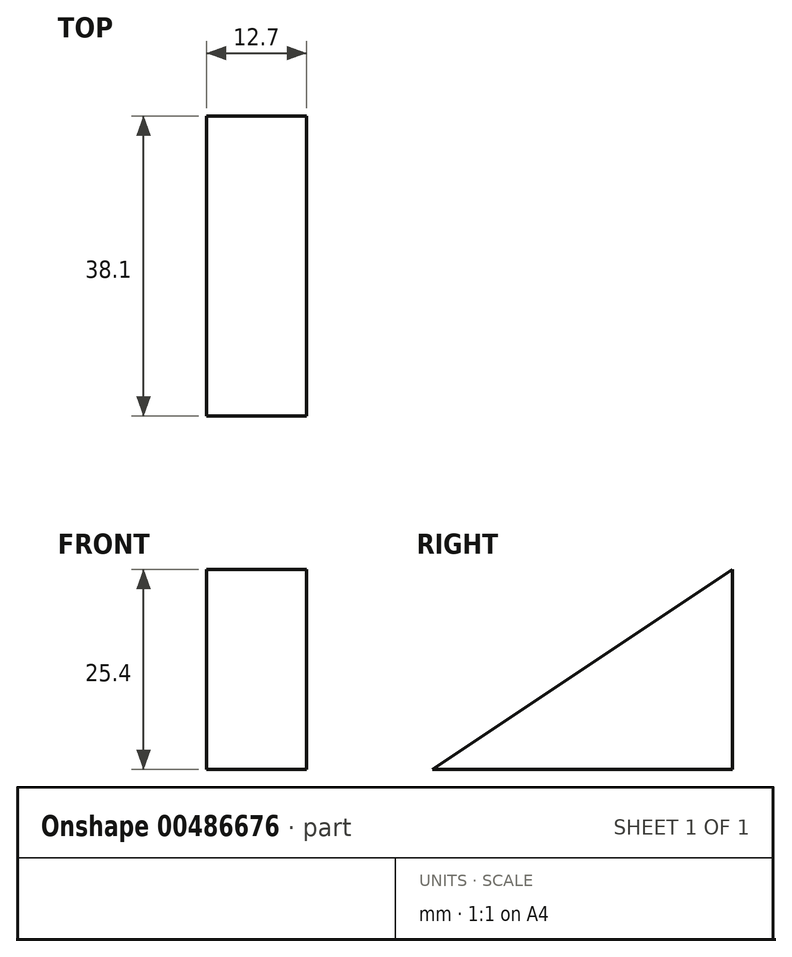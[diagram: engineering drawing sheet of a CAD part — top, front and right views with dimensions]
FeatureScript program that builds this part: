
annotation { "Feature Type Name" : "Feature", "Feature Type Description" : "" }
export const myFeature = defineFeature(function(context is Context, id is Id, definition is map)
    precondition{}
    {
        {
            var Q0;
            Q0=qCreatedBy(makeId("Right.planeOp"),FACE);
            var sketch = newSketch(context, id + "F0", { "sketchPlane" : qUnion([Q0])});
            skLineSegment(sketch, "E0", {"start": v(31.82, 9.68) * mm, "end": v(31.82, -15.72) * mm});
            skLineSegment(sketch, "E1", {"start": v(31.82, -15.72) * mm, "end": v(-6.28, -15.72) * mm});
            skLineSegment(sketch, "E2", {"start": v(-6.28, -15.72) * mm, "end": v(31.82, 9.68) * mm});
            skSolve(sketch);
        }
        {
            var Q0;
            Q0 = qSketchRegion(id + "F0", true);
            extrude(context, id + "F1", {"entities" : qUnion([Q0]), "depth" : 12.7 * mm});
        }
    });
